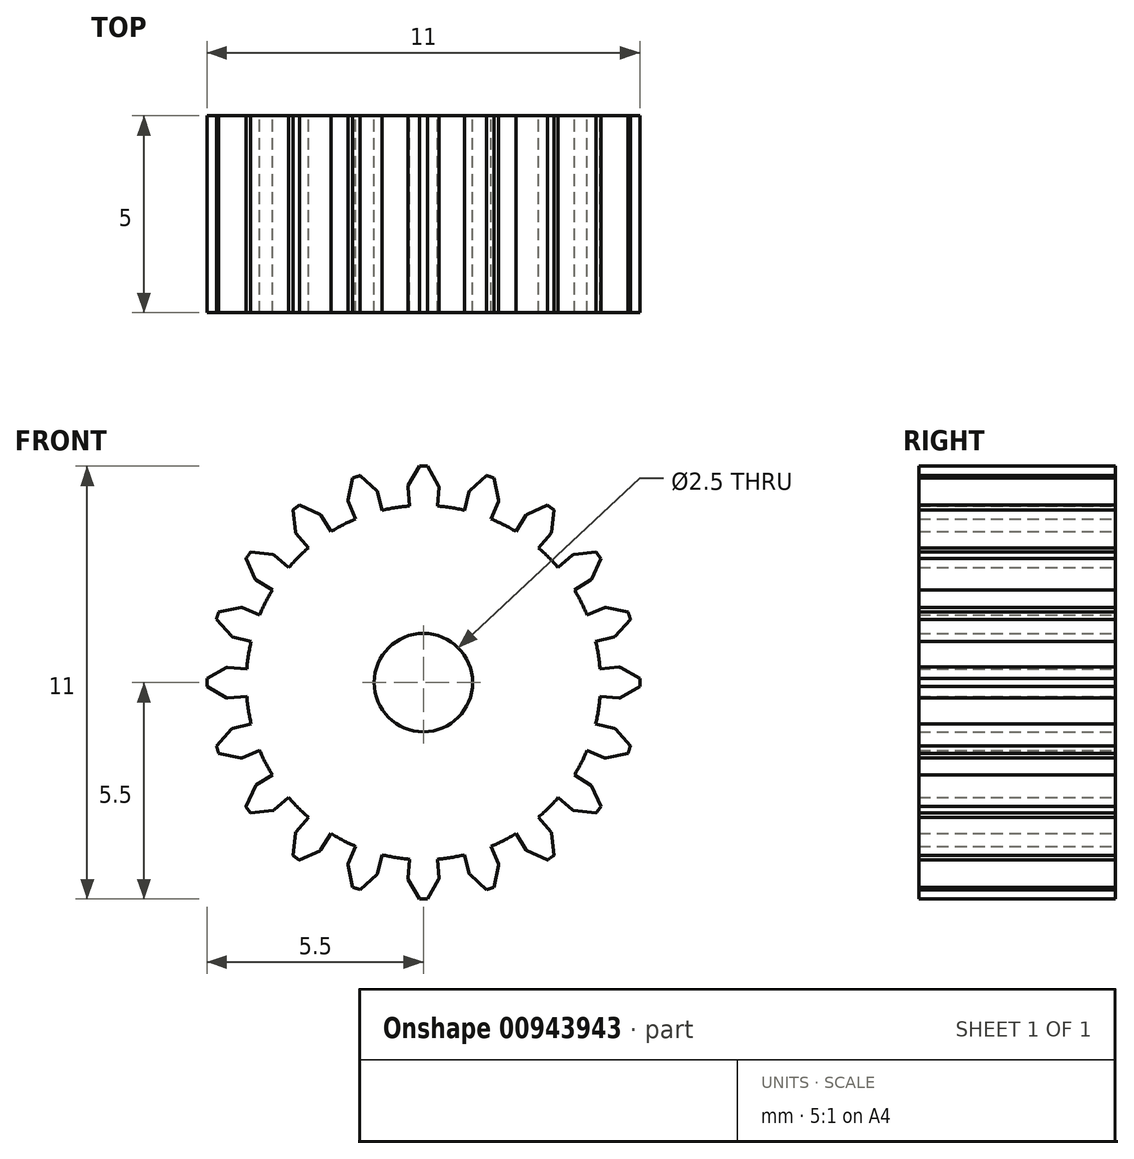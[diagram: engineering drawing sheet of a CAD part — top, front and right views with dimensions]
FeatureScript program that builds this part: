
annotation { "Feature Type Name" : "Feature", "Feature Type Description" : "" }
export const myFeature = defineFeature(function(context is Context, id is Id, definition is map)
    precondition{}
    {
        {
            var Q0;
            Q0=qCreatedBy(makeId("Front.planeOp"),FACE);
            var sketch = newSketch(context, id + "F0", { "sketchPlane" : qUnion([Q0])});
            skCircle(sketch, "E0", {"center": v(0, 0) * mm, "radius": 4.5 * mm});
            skCircle(sketch, "E1", {"center": v(0, 0) * mm, "radius": 5 * mm, "construction": true});
            skCircle(sketch, "E2", {"center": v(0, 0) * mm, "radius": 5.5 * mm, "construction": true});
            skLineSegment(sketch, "E3", {"start": v(0, 0) * mm, "end": v(1.46, 6.08) * mm, "construction": true});
            skArc(sketch, "E4", {"start": v(-0.4, 4.98) * mm, "mid": v(0, 5) * mm, "end": v(0.4, 4.98) * mm, "construction": true});
            skLineSegment(sketch, "E5", {"start": v(-0.35, 4.49) * mm, "end": v(-0.4, 4.98) * mm});
            skArc(sketch, "E6", {"start": v(0, 5.5) * mm, "mid": v(0.05, 5.5) * mm, "end": v(0.1, 5.5) * mm});
            skLineSegment(sketch, "E7", {"start": v(0.1, 5.5) * mm, "end": v(0.38, 5) * mm});
            skLineSegment(sketch, "E8", {"start": v(0.4, 4.98) * mm, "end": v(0.35, 4.49) * mm});
            skLineSegment(sketch, "E9", {"start": v(-0.38, 5) * mm, "end": v(-0.1, 5.5) * mm});
            skArc(sketch, "E10", {"start": v(-0.1, 5.5) * mm, "mid": v(-0.05, 5.5) * mm, "end": v(0, 5.5) * mm});
            skArc(sketch, "E11.filletArc", {"start": v(-0.38, 5) * mm, "mid": v(-0.4, 4.99) * mm, "end": v(-0.4, 4.97) * mm});
            skArc(sketch, "E12.filletArc", {"start": v(0.4, 4.97) * mm, "mid": v(0.4, 4.98) * mm, "end": v(0.38, 5) * mm});
            skLineSegment(sketch, "E13.1.0", {"start": v(-1.91, 4.64) * mm, "end": v(-1.8, 5.2) * mm});
            skLineSegment(sketch, "E13.1.1", {"start": v(-1.6, 5.26) * mm, "end": v(-1.18, 4.87) * mm});
            skArc(sketch, "E13.1.2", {"start": v(-1.8, 5.2) * mm, "mid": v(-1.75, 5.22) * mm, "end": v(-1.7, 5.23) * mm});
            skArc(sketch, "E13.1.3", {"start": v(-1.7, 5.23) * mm, "mid": v(-1.65, 5.25) * mm, "end": v(-1.6, 5.26) * mm});
            skArc(sketch, "E13.1.4", {"start": v(-1.16, 4.85) * mm, "mid": v(-1.17, 4.86) * mm, "end": v(-1.18, 4.87) * mm});
            skArc(sketch, "E13.1.5", {"start": v(-1.91, 4.64) * mm, "mid": v(-1.91, 4.62) * mm, "end": v(-1.9, 4.6) * mm});
            skLineSegment(sketch, "E13.1.6", {"start": v(0, 0) * mm, "end": v(-1.9, 4.6) * mm, "construction": true});
            skLineSegment(sketch, "E13.1.7", {"start": v(0, 0) * mm, "end": v(-1.16, 4.85) * mm, "construction": true});
            skLineSegment(sketch, "E13.2.0", {"start": v(-3.25, 3.82) * mm, "end": v(-3.31, 4.4) * mm});
            skLineSegment(sketch, "E13.2.1", {"start": v(-3.15, 4.5) * mm, "end": v(-2.63, 4.27) * mm});
            skArc(sketch, "E13.2.2", {"start": v(-3.31, 4.4) * mm, "mid": v(-3.27, 4.42) * mm, "end": v(-3.23, 4.45) * mm});
            skArc(sketch, "E13.2.3", {"start": v(-3.23, 4.45) * mm, "mid": v(-3.2, 4.48) * mm, "end": v(-3.15, 4.5) * mm});
            skArc(sketch, "E13.2.4", {"start": v(-2.6, 4.25) * mm, "mid": v(-2.61, 4.26) * mm, "end": v(-2.63, 4.27) * mm});
            skArc(sketch, "E13.2.5", {"start": v(-3.25, 3.82) * mm, "mid": v(-3.25, 3.8) * mm, "end": v(-3.24, 3.8) * mm});
            skLineSegment(sketch, "E13.2.6", {"start": v(0, 0) * mm, "end": v(-3.24, 3.8) * mm, "construction": true});
            skLineSegment(sketch, "E13.2.7", {"start": v(0, 0) * mm, "end": v(-2.6, 4.25) * mm, "construction": true});
            skLineSegment(sketch, "E13.3.0", {"start": v(-4.27, 2.63) * mm, "end": v(-4.5, 3.15) * mm});
            skLineSegment(sketch, "E13.3.1", {"start": v(-4.4, 3.31) * mm, "end": v(-3.82, 3.25) * mm});
            skArc(sketch, "E13.3.2", {"start": v(-4.5, 3.15) * mm, "mid": v(-4.48, 3.2) * mm, "end": v(-4.45, 3.23) * mm});
            skArc(sketch, "E13.3.3", {"start": v(-4.45, 3.23) * mm, "mid": v(-4.42, 3.27) * mm, "end": v(-4.4, 3.31) * mm});
            skArc(sketch, "E13.3.4", {"start": v(-3.8, 3.24) * mm, "mid": v(-3.8, 3.25) * mm, "end": v(-3.82, 3.25) * mm});
            skArc(sketch, "E13.3.5", {"start": v(-4.27, 2.63) * mm, "mid": v(-4.27, 2.62) * mm, "end": v(-4.25, 2.6) * mm});
            skLineSegment(sketch, "E13.3.6", {"start": v(0, 0) * mm, "end": v(-4.25, 2.6) * mm, "construction": true});
            skLineSegment(sketch, "E13.3.7", {"start": v(0, 0) * mm, "end": v(-3.8, 3.24) * mm, "construction": true});
            skLineSegment(sketch, "E13.4.0", {"start": v(-4.88, 1.18) * mm, "end": v(-5.26, 1.6) * mm});
            skLineSegment(sketch, "E13.4.1", {"start": v(-5.2, 1.8) * mm, "end": v(-4.63, 1.91) * mm});
            skArc(sketch, "E13.4.2", {"start": v(-5.26, 1.6) * mm, "mid": v(-5.25, 1.65) * mm, "end": v(-5.23, 1.7) * mm});
            skArc(sketch, "E13.4.3", {"start": v(-5.23, 1.7) * mm, "mid": v(-5.22, 1.75) * mm, "end": v(-5.2, 1.8) * mm});
            skArc(sketch, "E13.4.4", {"start": v(-4.6, 1.9) * mm, "mid": v(-4.62, 1.91) * mm, "end": v(-4.63, 1.91) * mm});
            skArc(sketch, "E13.4.5", {"start": v(-4.88, 1.18) * mm, "mid": v(-4.87, 1.17) * mm, "end": v(-4.85, 1.16) * mm});
            skLineSegment(sketch, "E13.4.6", {"start": v(0, 0) * mm, "end": v(-4.85, 1.16) * mm, "construction": true});
            skLineSegment(sketch, "E13.4.7", {"start": v(0, 0) * mm, "end": v(-4.6, 1.9) * mm, "construction": true});
            skLineSegment(sketch, "E13.5.0", {"start": v(-5, -0.38) * mm, "end": v(-5.5, -0.1) * mm});
            skLineSegment(sketch, "E13.5.1", {"start": v(-5.5, 0.1) * mm, "end": v(-5, 0.38) * mm});
            skArc(sketch, "E13.5.2", {"start": v(-5.5, -0.1) * mm, "mid": v(-5.5, -0.05) * mm, "end": v(-5.5, 0) * mm});
            skArc(sketch, "E13.5.3", {"start": v(-5.5, 0) * mm, "mid": v(-5.5, 0.05) * mm, "end": v(-5.5, 0.1) * mm});
            skArc(sketch, "E13.5.4", {"start": v(-4.97, 0.4) * mm, "mid": v(-4.98, 0.4) * mm, "end": v(-5, 0.38) * mm});
            skArc(sketch, "E13.5.5", {"start": v(-5, -0.38) * mm, "mid": v(-4.99, -0.4) * mm, "end": v(-4.97, -0.4) * mm});
            skLineSegment(sketch, "E13.5.6", {"start": v(0, 0) * mm, "end": v(-4.97, -0.4) * mm, "construction": true});
            skLineSegment(sketch, "E13.5.7", {"start": v(0, 0) * mm, "end": v(-4.97, 0.4) * mm, "construction": true});
            skLineSegment(sketch, "E13.6.0", {"start": v(-4.64, -1.91) * mm, "end": v(-5.2, -1.8) * mm});
            skLineSegment(sketch, "E13.6.1", {"start": v(-5.26, -1.6) * mm, "end": v(-4.87, -1.18) * mm});
            skArc(sketch, "E13.6.2", {"start": v(-5.2, -1.8) * mm, "mid": v(-5.22, -1.75) * mm, "end": v(-5.23, -1.7) * mm});
            skArc(sketch, "E13.6.3", {"start": v(-5.23, -1.7) * mm, "mid": v(-5.25, -1.65) * mm, "end": v(-5.26, -1.6) * mm});
            skArc(sketch, "E13.6.4", {"start": v(-4.85, -1.16) * mm, "mid": v(-4.86, -1.17) * mm, "end": v(-4.87, -1.18) * mm});
            skArc(sketch, "E13.6.5", {"start": v(-4.64, -1.91) * mm, "mid": v(-4.62, -1.91) * mm, "end": v(-4.6, -1.9) * mm});
            skLineSegment(sketch, "E13.6.6", {"start": v(0, 0) * mm, "end": v(-4.6, -1.9) * mm, "construction": true});
            skLineSegment(sketch, "E13.6.7", {"start": v(0, 0) * mm, "end": v(-4.85, -1.16) * mm, "construction": true});
            skLineSegment(sketch, "E13.7.0", {"start": v(-3.82, -3.25) * mm, "end": v(-4.4, -3.31) * mm});
            skLineSegment(sketch, "E13.7.1", {"start": v(-4.5, -3.15) * mm, "end": v(-4.27, -2.63) * mm});
            skArc(sketch, "E13.7.2", {"start": v(-4.4, -3.31) * mm, "mid": v(-4.42, -3.27) * mm, "end": v(-4.45, -3.23) * mm});
            skArc(sketch, "E13.7.3", {"start": v(-4.45, -3.23) * mm, "mid": v(-4.48, -3.2) * mm, "end": v(-4.5, -3.15) * mm});
            skArc(sketch, "E13.7.4", {"start": v(-4.25, -2.6) * mm, "mid": v(-4.26, -2.61) * mm, "end": v(-4.27, -2.63) * mm});
            skArc(sketch, "E13.7.5", {"start": v(-3.82, -3.25) * mm, "mid": v(-3.8, -3.25) * mm, "end": v(-3.8, -3.24) * mm});
            skLineSegment(sketch, "E13.7.6", {"start": v(0, 0) * mm, "end": v(-3.8, -3.24) * mm, "construction": true});
            skLineSegment(sketch, "E13.7.7", {"start": v(0, 0) * mm, "end": v(-4.25, -2.6) * mm, "construction": true});
            skLineSegment(sketch, "E13.8.0", {"start": v(-2.63, -4.27) * mm, "end": v(-3.15, -4.5) * mm});
            skLineSegment(sketch, "E13.8.1", {"start": v(-3.31, -4.4) * mm, "end": v(-3.25, -3.82) * mm});
            skArc(sketch, "E13.8.2", {"start": v(-3.15, -4.5) * mm, "mid": v(-3.2, -4.48) * mm, "end": v(-3.23, -4.45) * mm});
            skArc(sketch, "E13.8.3", {"start": v(-3.23, -4.45) * mm, "mid": v(-3.27, -4.42) * mm, "end": v(-3.31, -4.4) * mm});
            skArc(sketch, "E13.8.4", {"start": v(-3.24, -3.8) * mm, "mid": v(-3.25, -3.8) * mm, "end": v(-3.25, -3.82) * mm});
            skArc(sketch, "E13.8.5", {"start": v(-2.63, -4.27) * mm, "mid": v(-2.62, -4.27) * mm, "end": v(-2.6, -4.25) * mm});
            skLineSegment(sketch, "E13.8.6", {"start": v(0, 0) * mm, "end": v(-2.6, -4.25) * mm, "construction": true});
            skLineSegment(sketch, "E13.8.7", {"start": v(0, 0) * mm, "end": v(-3.24, -3.8) * mm, "construction": true});
            skLineSegment(sketch, "E13.9.0", {"start": v(-1.18, -4.88) * mm, "end": v(-1.6, -5.26) * mm});
            skLineSegment(sketch, "E13.9.1", {"start": v(-1.8, -5.2) * mm, "end": v(-1.91, -4.63) * mm});
            skArc(sketch, "E13.9.2", {"start": v(-1.6, -5.26) * mm, "mid": v(-1.65, -5.25) * mm, "end": v(-1.7, -5.23) * mm});
            skArc(sketch, "E13.9.3", {"start": v(-1.7, -5.23) * mm, "mid": v(-1.75, -5.22) * mm, "end": v(-1.8, -5.2) * mm});
            skArc(sketch, "E13.9.4", {"start": v(-1.9, -4.6) * mm, "mid": v(-1.91, -4.62) * mm, "end": v(-1.91, -4.63) * mm});
            skArc(sketch, "E13.9.5", {"start": v(-1.18, -4.88) * mm, "mid": v(-1.17, -4.87) * mm, "end": v(-1.16, -4.85) * mm});
            skLineSegment(sketch, "E13.9.6", {"start": v(0, 0) * mm, "end": v(-1.16, -4.85) * mm, "construction": true});
            skLineSegment(sketch, "E13.9.7", {"start": v(0, 0) * mm, "end": v(-1.9, -4.6) * mm, "construction": true});
            skLineSegment(sketch, "E13.10.0", {"start": v(0.38, -5) * mm, "end": v(0.1, -5.5) * mm});
            skLineSegment(sketch, "E13.10.1", {"start": v(-0.1, -5.5) * mm, "end": v(-0.38, -5) * mm});
            skArc(sketch, "E13.10.2", {"start": v(0.1, -5.5) * mm, "mid": v(0.05, -5.5) * mm, "end": v(0, -5.5) * mm});
            skArc(sketch, "E13.10.3", {"start": v(0, -5.5) * mm, "mid": v(-0.05, -5.5) * mm, "end": v(-0.1, -5.5) * mm});
            skArc(sketch, "E13.10.4", {"start": v(-0.4, -4.97) * mm, "mid": v(-0.4, -4.98) * mm, "end": v(-0.38, -5) * mm});
            skArc(sketch, "E13.10.5", {"start": v(0.38, -5) * mm, "mid": v(0.4, -4.99) * mm, "end": v(0.4, -4.97) * mm});
            skLineSegment(sketch, "E13.10.6", {"start": v(0, 0) * mm, "end": v(0.4, -4.97) * mm, "construction": true});
            skLineSegment(sketch, "E13.10.7", {"start": v(0, 0) * mm, "end": v(-0.4, -4.97) * mm, "construction": true});
            skLineSegment(sketch, "E13.11.0", {"start": v(1.91, -4.64) * mm, "end": v(1.8, -5.2) * mm});
            skLineSegment(sketch, "E13.11.1", {"start": v(1.6, -5.26) * mm, "end": v(1.18, -4.87) * mm});
            skArc(sketch, "E13.11.2", {"start": v(1.8, -5.2) * mm, "mid": v(1.75, -5.22) * mm, "end": v(1.7, -5.23) * mm});
            skArc(sketch, "E13.11.3", {"start": v(1.7, -5.23) * mm, "mid": v(1.65, -5.25) * mm, "end": v(1.6, -5.26) * mm});
            skArc(sketch, "E13.11.4", {"start": v(1.16, -4.85) * mm, "mid": v(1.17, -4.86) * mm, "end": v(1.18, -4.87) * mm});
            skArc(sketch, "E13.11.5", {"start": v(1.91, -4.64) * mm, "mid": v(1.91, -4.62) * mm, "end": v(1.9, -4.6) * mm});
            skLineSegment(sketch, "E13.11.6", {"start": v(0, 0) * mm, "end": v(1.9, -4.6) * mm, "construction": true});
            skLineSegment(sketch, "E13.11.7", {"start": v(0, 0) * mm, "end": v(1.16, -4.85) * mm, "construction": true});
            skLineSegment(sketch, "E13.12.0", {"start": v(3.25, -3.82) * mm, "end": v(3.31, -4.4) * mm});
            skLineSegment(sketch, "E13.12.1", {"start": v(3.15, -4.5) * mm, "end": v(2.63, -4.27) * mm});
            skArc(sketch, "E13.12.2", {"start": v(3.31, -4.4) * mm, "mid": v(3.27, -4.42) * mm, "end": v(3.23, -4.45) * mm});
            skArc(sketch, "E13.12.3", {"start": v(3.23, -4.45) * mm, "mid": v(3.2, -4.48) * mm, "end": v(3.15, -4.5) * mm});
            skArc(sketch, "E13.12.4", {"start": v(2.6, -4.25) * mm, "mid": v(2.61, -4.26) * mm, "end": v(2.63, -4.27) * mm});
            skArc(sketch, "E13.12.5", {"start": v(3.25, -3.82) * mm, "mid": v(3.25, -3.8) * mm, "end": v(3.24, -3.8) * mm});
            skLineSegment(sketch, "E13.12.6", {"start": v(0, 0) * mm, "end": v(3.24, -3.8) * mm, "construction": true});
            skLineSegment(sketch, "E13.12.7", {"start": v(0, 0) * mm, "end": v(2.6, -4.25) * mm, "construction": true});
            skLineSegment(sketch, "E13.13.0", {"start": v(4.27, -2.63) * mm, "end": v(4.5, -3.15) * mm});
            skLineSegment(sketch, "E13.13.1", {"start": v(4.4, -3.31) * mm, "end": v(3.82, -3.25) * mm});
            skArc(sketch, "E13.13.2", {"start": v(4.5, -3.15) * mm, "mid": v(4.48, -3.2) * mm, "end": v(4.45, -3.23) * mm});
            skArc(sketch, "E13.13.3", {"start": v(4.45, -3.23) * mm, "mid": v(4.42, -3.27) * mm, "end": v(4.4, -3.31) * mm});
            skArc(sketch, "E13.13.4", {"start": v(3.8, -3.24) * mm, "mid": v(3.8, -3.25) * mm, "end": v(3.82, -3.25) * mm});
            skArc(sketch, "E13.13.5", {"start": v(4.27, -2.63) * mm, "mid": v(4.27, -2.62) * mm, "end": v(4.25, -2.6) * mm});
            skLineSegment(sketch, "E13.13.6", {"start": v(0, 0) * mm, "end": v(4.25, -2.6) * mm, "construction": true});
            skLineSegment(sketch, "E13.13.7", {"start": v(0, 0) * mm, "end": v(3.8, -3.24) * mm, "construction": true});
            skLineSegment(sketch, "E13.14.0", {"start": v(4.88, -1.18) * mm, "end": v(5.26, -1.6) * mm});
            skLineSegment(sketch, "E13.14.1", {"start": v(5.2, -1.8) * mm, "end": v(4.63, -1.91) * mm});
            skArc(sketch, "E13.14.2", {"start": v(5.26, -1.6) * mm, "mid": v(5.25, -1.65) * mm, "end": v(5.23, -1.7) * mm});
            skArc(sketch, "E13.14.3", {"start": v(5.23, -1.7) * mm, "mid": v(5.22, -1.75) * mm, "end": v(5.2, -1.8) * mm});
            skArc(sketch, "E13.14.4", {"start": v(4.6, -1.9) * mm, "mid": v(4.62, -1.91) * mm, "end": v(4.63, -1.91) * mm});
            skArc(sketch, "E13.14.5", {"start": v(4.88, -1.18) * mm, "mid": v(4.87, -1.17) * mm, "end": v(4.85, -1.16) * mm});
            skLineSegment(sketch, "E13.14.6", {"start": v(0, 0) * mm, "end": v(4.85, -1.16) * mm, "construction": true});
            skLineSegment(sketch, "E13.14.7", {"start": v(0, 0) * mm, "end": v(4.6, -1.9) * mm, "construction": true});
            skLineSegment(sketch, "E13.15.0", {"start": v(5, 0.38) * mm, "end": v(5.5, 0.1) * mm});
            skLineSegment(sketch, "E13.15.1", {"start": v(5.5, -0.1) * mm, "end": v(5, -0.38) * mm});
            skArc(sketch, "E13.15.2", {"start": v(5.5, 0.1) * mm, "mid": v(5.5, 0.05) * mm, "end": v(5.5, 0) * mm});
            skArc(sketch, "E13.15.3", {"start": v(5.5, 0) * mm, "mid": v(5.5, -0.05) * mm, "end": v(5.5, -0.1) * mm});
            skArc(sketch, "E13.15.4", {"start": v(4.97, -0.4) * mm, "mid": v(4.98, -0.4) * mm, "end": v(5, -0.38) * mm});
            skArc(sketch, "E13.15.5", {"start": v(5, 0.38) * mm, "mid": v(4.99, 0.4) * mm, "end": v(4.97, 0.4) * mm});
            skLineSegment(sketch, "E13.15.6", {"start": v(0, 0) * mm, "end": v(4.97, 0.4) * mm, "construction": true});
            skLineSegment(sketch, "E13.15.7", {"start": v(0, 0) * mm, "end": v(4.97, -0.4) * mm, "construction": true});
            skLineSegment(sketch, "E13.16.0", {"start": v(4.64, 1.91) * mm, "end": v(5.2, 1.8) * mm});
            skLineSegment(sketch, "E13.16.1", {"start": v(5.26, 1.6) * mm, "end": v(4.87, 1.18) * mm});
            skArc(sketch, "E13.16.2", {"start": v(5.2, 1.8) * mm, "mid": v(5.22, 1.75) * mm, "end": v(5.23, 1.7) * mm});
            skArc(sketch, "E13.16.3", {"start": v(5.23, 1.7) * mm, "mid": v(5.25, 1.65) * mm, "end": v(5.26, 1.6) * mm});
            skArc(sketch, "E13.16.4", {"start": v(4.85, 1.16) * mm, "mid": v(4.86, 1.17) * mm, "end": v(4.87, 1.18) * mm});
            skArc(sketch, "E13.16.5", {"start": v(4.64, 1.91) * mm, "mid": v(4.62, 1.91) * mm, "end": v(4.6, 1.9) * mm});
            skLineSegment(sketch, "E13.16.6", {"start": v(0, 0) * mm, "end": v(4.6, 1.9) * mm, "construction": true});
            skLineSegment(sketch, "E13.16.7", {"start": v(0, 0) * mm, "end": v(4.85, 1.16) * mm, "construction": true});
            skLineSegment(sketch, "E13.17.0", {"start": v(3.82, 3.25) * mm, "end": v(4.4, 3.31) * mm});
            skLineSegment(sketch, "E13.17.1", {"start": v(4.5, 3.15) * mm, "end": v(4.27, 2.63) * mm});
            skArc(sketch, "E13.17.2", {"start": v(4.4, 3.31) * mm, "mid": v(4.42, 3.27) * mm, "end": v(4.45, 3.23) * mm});
            skArc(sketch, "E13.17.3", {"start": v(4.45, 3.23) * mm, "mid": v(4.48, 3.2) * mm, "end": v(4.5, 3.15) * mm});
            skArc(sketch, "E13.17.4", {"start": v(4.25, 2.6) * mm, "mid": v(4.26, 2.61) * mm, "end": v(4.27, 2.63) * mm});
            skArc(sketch, "E13.17.5", {"start": v(3.82, 3.25) * mm, "mid": v(3.8, 3.25) * mm, "end": v(3.8, 3.24) * mm});
            skLineSegment(sketch, "E13.17.6", {"start": v(0, 0) * mm, "end": v(3.8, 3.24) * mm, "construction": true});
            skLineSegment(sketch, "E13.17.7", {"start": v(0, 0) * mm, "end": v(4.25, 2.6) * mm, "construction": true});
            skLineSegment(sketch, "E13.18.0", {"start": v(2.63, 4.27) * mm, "end": v(3.15, 4.5) * mm});
            skLineSegment(sketch, "E13.18.1", {"start": v(3.31, 4.4) * mm, "end": v(3.25, 3.82) * mm});
            skArc(sketch, "E13.18.2", {"start": v(3.15, 4.5) * mm, "mid": v(3.2, 4.48) * mm, "end": v(3.23, 4.45) * mm});
            skArc(sketch, "E13.18.3", {"start": v(3.23, 4.45) * mm, "mid": v(3.27, 4.42) * mm, "end": v(3.31, 4.4) * mm});
            skArc(sketch, "E13.18.4", {"start": v(3.24, 3.8) * mm, "mid": v(3.25, 3.8) * mm, "end": v(3.25, 3.82) * mm});
            skArc(sketch, "E13.18.5", {"start": v(2.63, 4.27) * mm, "mid": v(2.62, 4.27) * mm, "end": v(2.6, 4.25) * mm});
            skLineSegment(sketch, "E13.18.6", {"start": v(0, 0) * mm, "end": v(2.6, 4.25) * mm, "construction": true});
            skLineSegment(sketch, "E13.18.7", {"start": v(0, 0) * mm, "end": v(3.24, 3.8) * mm, "construction": true});
            skLineSegment(sketch, "E13.19.0", {"start": v(1.18, 4.88) * mm, "end": v(1.6, 5.26) * mm});
            skLineSegment(sketch, "E13.19.1", {"start": v(1.8, 5.2) * mm, "end": v(1.91, 4.63) * mm});
            skArc(sketch, "E13.19.2", {"start": v(1.6, 5.26) * mm, "mid": v(1.65, 5.25) * mm, "end": v(1.7, 5.23) * mm});
            skArc(sketch, "E13.19.3", {"start": v(1.7, 5.23) * mm, "mid": v(1.75, 5.22) * mm, "end": v(1.8, 5.2) * mm});
            skArc(sketch, "E13.19.4", {"start": v(1.9, 4.6) * mm, "mid": v(1.91, 4.62) * mm, "end": v(1.91, 4.63) * mm});
            skArc(sketch, "E13.19.5", {"start": v(1.18, 4.88) * mm, "mid": v(1.17, 4.87) * mm, "end": v(1.16, 4.85) * mm});
            skLineSegment(sketch, "E13.19.6", {"start": v(0, 0) * mm, "end": v(1.16, 4.85) * mm, "construction": true});
            skLineSegment(sketch, "E13.19.7", {"start": v(0, 0) * mm, "end": v(1.9, 4.6) * mm, "construction": true});
            skLineSegment(sketch, "E14.1.0", {"start": v(-1.72, 4.16) * mm, "end": v(-1.91, 4.62) * mm});
            skLineSegment(sketch, "E14.1.1", {"start": v(-1.17, 4.86) * mm, "end": v(-1.05, 4.38) * mm});
            skLineSegment(sketch, "E14.2.0", {"start": v(-2.92, 3.42) * mm, "end": v(-3.25, 3.8) * mm});
            skLineSegment(sketch, "E14.2.1", {"start": v(-2.61, 4.26) * mm, "end": v(-2.35, 3.84) * mm});
            skLineSegment(sketch, "E14.3.0", {"start": v(-3.84, 2.35) * mm, "end": v(-4.26, 2.61) * mm});
            skLineSegment(sketch, "E14.3.1", {"start": v(-3.8, 3.25) * mm, "end": v(-3.42, 2.92) * mm});
            skLineSegment(sketch, "E14.4.0", {"start": v(-4.38, 1.05) * mm, "end": v(-4.86, 1.17) * mm});
            skLineSegment(sketch, "E14.4.1", {"start": v(-4.62, 1.91) * mm, "end": v(-4.16, 1.72) * mm});
            skLineSegment(sketch, "E14.5.0", {"start": v(-4.49, -0.35) * mm, "end": v(-4.98, -0.4) * mm});
            skLineSegment(sketch, "E14.5.1", {"start": v(-4.98, 0.4) * mm, "end": v(-4.49, 0.35) * mm});
            skLineSegment(sketch, "E14.6.0", {"start": v(-4.16, -1.72) * mm, "end": v(-4.62, -1.91) * mm});
            skLineSegment(sketch, "E14.6.1", {"start": v(-4.86, -1.17) * mm, "end": v(-4.38, -1.05) * mm});
            skLineSegment(sketch, "E14.7.0", {"start": v(-3.42, -2.92) * mm, "end": v(-3.8, -3.25) * mm});
            skLineSegment(sketch, "E14.7.1", {"start": v(-4.26, -2.61) * mm, "end": v(-3.84, -2.35) * mm});
            skLineSegment(sketch, "E14.8.0", {"start": v(-2.35, -3.84) * mm, "end": v(-2.61, -4.26) * mm});
            skLineSegment(sketch, "E14.8.1", {"start": v(-3.25, -3.8) * mm, "end": v(-2.92, -3.42) * mm});
            skLineSegment(sketch, "E14.9.0", {"start": v(-1.05, -4.38) * mm, "end": v(-1.17, -4.86) * mm});
            skLineSegment(sketch, "E14.9.1", {"start": v(-1.91, -4.62) * mm, "end": v(-1.72, -4.16) * mm});
            skLineSegment(sketch, "E14.10.0", {"start": v(0.35, -4.49) * mm, "end": v(0.4, -4.98) * mm});
            skLineSegment(sketch, "E14.10.1", {"start": v(-0.4, -4.98) * mm, "end": v(-0.35, -4.49) * mm});
            skLineSegment(sketch, "E14.11.0", {"start": v(1.72, -4.16) * mm, "end": v(1.91, -4.62) * mm});
            skLineSegment(sketch, "E14.11.1", {"start": v(1.17, -4.86) * mm, "end": v(1.05, -4.38) * mm});
            skLineSegment(sketch, "E14.12.0", {"start": v(2.92, -3.42) * mm, "end": v(3.25, -3.8) * mm});
            skLineSegment(sketch, "E14.12.1", {"start": v(2.61, -4.26) * mm, "end": v(2.35, -3.84) * mm});
            skLineSegment(sketch, "E14.13.0", {"start": v(3.84, -2.35) * mm, "end": v(4.26, -2.61) * mm});
            skLineSegment(sketch, "E14.13.1", {"start": v(3.8, -3.25) * mm, "end": v(3.42, -2.92) * mm});
            skLineSegment(sketch, "E14.14.0", {"start": v(4.38, -1.05) * mm, "end": v(4.86, -1.17) * mm});
            skLineSegment(sketch, "E14.14.1", {"start": v(4.62, -1.91) * mm, "end": v(4.16, -1.72) * mm});
            skLineSegment(sketch, "E14.15.0", {"start": v(4.49, 0.35) * mm, "end": v(4.98, 0.4) * mm});
            skLineSegment(sketch, "E14.15.1", {"start": v(4.98, -0.4) * mm, "end": v(4.49, -0.35) * mm});
            skLineSegment(sketch, "E14.16.0", {"start": v(4.16, 1.72) * mm, "end": v(4.62, 1.91) * mm});
            skLineSegment(sketch, "E14.16.1", {"start": v(4.86, 1.17) * mm, "end": v(4.38, 1.05) * mm});
            skLineSegment(sketch, "E14.17.0", {"start": v(3.42, 2.92) * mm, "end": v(3.8, 3.25) * mm});
            skLineSegment(sketch, "E14.17.1", {"start": v(4.26, 2.61) * mm, "end": v(3.84, 2.35) * mm});
            skLineSegment(sketch, "E14.18.0", {"start": v(2.35, 3.84) * mm, "end": v(2.61, 4.26) * mm});
            skLineSegment(sketch, "E14.18.1", {"start": v(3.25, 3.8) * mm, "end": v(2.92, 3.42) * mm});
            skLineSegment(sketch, "E14.19.0", {"start": v(1.05, 4.38) * mm, "end": v(1.17, 4.86) * mm});
            skLineSegment(sketch, "E14.19.1", {"start": v(1.91, 4.62) * mm, "end": v(1.72, 4.16) * mm});
            skSolve(sketch);
        }
        {
            var Q0;
            Q0 = qSketchRegion(id + "F0", true);
            extrude(context, id + "F1", {"entities" : qUnion([Q0]), "depth" : 5 * mm, "offsetDistance" : 25 * mm});
        }
        {
            var Q0;
            Q0=sQuery(id+"F0.wireOp",VERTEX,"E0.center");
            var Q1;
            Q1=makeQuery(id+"F1.opExtrude","SWEPT_BODY",BODY,{"disambiguationData":[OSD([sQuery(id+"F0.wireOp",EDGE,"E0"),sQuery(id+"F0.wireOp",EDGE,"E5"),sQuery(id+"F0.wireOp",EDGE,"E6"),sQuery(id+"F0.wireOp",EDGE,"E7"),sQuery(id+"F0.wireOp",EDGE,"E8"),sQuery(id+"F0.wireOp",EDGE,"E9"),sQuery(id+"F0.wireOp",EDGE,"E10"),sQuery(id+"F0.wireOp",EDGE,"E11.filletArc"),sQuery(id+"F0.wireOp",EDGE,"E12.filletArc"),sQuery(id+"F0.wireOp",EDGE,"E13.1.0"),sQuery(id+"F0.wireOp",EDGE,"E13.1.1"),sQuery(id+"F0.wireOp",EDGE,"E13.1.2"),sQuery(id+"F0.wireOp",EDGE,"E13.1.3"),sQuery(id+"F0.wireOp",EDGE,"E13.1.4"),sQuery(id+"F0.wireOp",EDGE,"E13.1.5"),sQuery(id+"F0.wireOp",EDGE,"E13.2.0"),sQuery(id+"F0.wireOp",EDGE,"E13.2.1"),sQuery(id+"F0.wireOp",EDGE,"E13.2.2"),sQuery(id+"F0.wireOp",EDGE,"E13.2.3"),sQuery(id+"F0.wireOp",EDGE,"E13.2.4"),sQuery(id+"F0.wireOp",EDGE,"E13.2.5"),sQuery(id+"F0.wireOp",EDGE,"E13.3.0"),sQuery(id+"F0.wireOp",EDGE,"E13.3.1"),sQuery(id+"F0.wireOp",EDGE,"E13.3.2"),sQuery(id+"F0.wireOp",EDGE,"E13.3.3"),sQuery(id+"F0.wireOp",EDGE,"E13.3.4"),sQuery(id+"F0.wireOp",EDGE,"E13.3.5"),sQuery(id+"F0.wireOp",EDGE,"E13.4.0"),sQuery(id+"F0.wireOp",EDGE,"E13.4.1"),sQuery(id+"F0.wireOp",EDGE,"E13.4.2"),sQuery(id+"F0.wireOp",EDGE,"E13.4.3"),sQuery(id+"F0.wireOp",EDGE,"E13.4.4"),sQuery(id+"F0.wireOp",EDGE,"E13.4.5"),sQuery(id+"F0.wireOp",EDGE,"E13.5.0"),sQuery(id+"F0.wireOp",EDGE,"E13.5.1"),sQuery(id+"F0.wireOp",EDGE,"E13.5.2"),sQuery(id+"F0.wireOp",EDGE,"E13.5.3"),sQuery(id+"F0.wireOp",EDGE,"E13.5.4"),sQuery(id+"F0.wireOp",EDGE,"E13.5.5"),sQuery(id+"F0.wireOp",EDGE,"E13.6.0"),sQuery(id+"F0.wireOp",EDGE,"E13.6.1"),sQuery(id+"F0.wireOp",EDGE,"E13.6.2"),sQuery(id+"F0.wireOp",EDGE,"E13.6.3"),sQuery(id+"F0.wireOp",EDGE,"E13.6.4"),sQuery(id+"F0.wireOp",EDGE,"E13.6.5"),sQuery(id+"F0.wireOp",EDGE,"E13.7.0"),sQuery(id+"F0.wireOp",EDGE,"E13.7.1"),sQuery(id+"F0.wireOp",EDGE,"E13.7.2"),sQuery(id+"F0.wireOp",EDGE,"E13.7.3"),sQuery(id+"F0.wireOp",EDGE,"E13.7.4"),sQuery(id+"F0.wireOp",EDGE,"E13.7.5"),sQuery(id+"F0.wireOp",EDGE,"E13.8.0"),sQuery(id+"F0.wireOp",EDGE,"E13.8.1"),sQuery(id+"F0.wireOp",EDGE,"E13.8.2"),sQuery(id+"F0.wireOp",EDGE,"E13.8.3"),sQuery(id+"F0.wireOp",EDGE,"E13.8.4"),sQuery(id+"F0.wireOp",EDGE,"E13.8.5"),sQuery(id+"F0.wireOp",EDGE,"E13.9.0"),sQuery(id+"F0.wireOp",EDGE,"E13.9.1"),sQuery(id+"F0.wireOp",EDGE,"E13.9.2"),sQuery(id+"F0.wireOp",EDGE,"E13.9.3"),sQuery(id+"F0.wireOp",EDGE,"E13.9.4"),sQuery(id+"F0.wireOp",EDGE,"E13.9.5"),sQuery(id+"F0.wireOp",EDGE,"E13.10.0"),sQuery(id+"F0.wireOp",EDGE,"E13.10.1"),sQuery(id+"F0.wireOp",EDGE,"E13.10.2"),sQuery(id+"F0.wireOp",EDGE,"E13.10.3"),sQuery(id+"F0.wireOp",EDGE,"E13.10.4"),sQuery(id+"F0.wireOp",EDGE,"E13.10.5"),sQuery(id+"F0.wireOp",EDGE,"E13.11.0"),sQuery(id+"F0.wireOp",EDGE,"E13.11.1"),sQuery(id+"F0.wireOp",EDGE,"E13.11.2"),sQuery(id+"F0.wireOp",EDGE,"E13.11.3"),sQuery(id+"F0.wireOp",EDGE,"E13.11.4"),sQuery(id+"F0.wireOp",EDGE,"E13.11.5"),sQuery(id+"F0.wireOp",EDGE,"E13.12.0"),sQuery(id+"F0.wireOp",EDGE,"E13.12.1"),sQuery(id+"F0.wireOp",EDGE,"E13.12.2"),sQuery(id+"F0.wireOp",EDGE,"E13.12.3"),sQuery(id+"F0.wireOp",EDGE,"E13.12.4"),sQuery(id+"F0.wireOp",EDGE,"E13.12.5"),sQuery(id+"F0.wireOp",EDGE,"E13.13.0"),sQuery(id+"F0.wireOp",EDGE,"E13.13.1"),sQuery(id+"F0.wireOp",EDGE,"E13.13.2"),sQuery(id+"F0.wireOp",EDGE,"E13.13.3"),sQuery(id+"F0.wireOp",EDGE,"E13.13.4"),sQuery(id+"F0.wireOp",EDGE,"E13.13.5"),sQuery(id+"F0.wireOp",EDGE,"E13.14.0"),sQuery(id+"F0.wireOp",EDGE,"E13.14.1"),sQuery(id+"F0.wireOp",EDGE,"E13.14.2"),sQuery(id+"F0.wireOp",EDGE,"E13.14.3"),sQuery(id+"F0.wireOp",EDGE,"E13.14.4"),sQuery(id+"F0.wireOp",EDGE,"E13.14.5"),sQuery(id+"F0.wireOp",EDGE,"E13.15.0"),sQuery(id+"F0.wireOp",EDGE,"E13.15.1"),sQuery(id+"F0.wireOp",EDGE,"E13.15.2"),sQuery(id+"F0.wireOp",EDGE,"E13.15.3"),sQuery(id+"F0.wireOp",EDGE,"E13.15.4"),sQuery(id+"F0.wireOp",EDGE,"E13.15.5"),sQuery(id+"F0.wireOp",EDGE,"E13.16.0"),sQuery(id+"F0.wireOp",EDGE,"E13.16.1"),sQuery(id+"F0.wireOp",EDGE,"E13.16.2"),sQuery(id+"F0.wireOp",EDGE,"E13.16.3"),sQuery(id+"F0.wireOp",EDGE,"E13.16.4"),sQuery(id+"F0.wireOp",EDGE,"E13.16.5"),sQuery(id+"F0.wireOp",EDGE,"E13.17.0"),sQuery(id+"F0.wireOp",EDGE,"E13.17.1"),sQuery(id+"F0.wireOp",EDGE,"E13.17.2"),sQuery(id+"F0.wireOp",EDGE,"E13.17.3"),sQuery(id+"F0.wireOp",EDGE,"E13.17.4"),sQuery(id+"F0.wireOp",EDGE,"E13.17.5"),sQuery(id+"F0.wireOp",EDGE,"E13.18.0"),sQuery(id+"F0.wireOp",EDGE,"E13.18.1"),sQuery(id+"F0.wireOp",EDGE,"E13.18.2"),sQuery(id+"F0.wireOp",EDGE,"E13.18.3"),sQuery(id+"F0.wireOp",EDGE,"E13.18.4"),sQuery(id+"F0.wireOp",EDGE,"E13.18.5"),sQuery(id+"F0.wireOp",EDGE,"E13.19.0"),sQuery(id+"F0.wireOp",EDGE,"E13.19.1"),sQuery(id+"F0.wireOp",EDGE,"E13.19.2"),sQuery(id+"F0.wireOp",EDGE,"E13.19.3"),sQuery(id+"F0.wireOp",EDGE,"E13.19.4"),sQuery(id+"F0.wireOp",EDGE,"E13.19.5"),sQuery(id+"F0.wireOp",EDGE,"E14.1.0"),sQuery(id+"F0.wireOp",EDGE,"E14.1.1"),sQuery(id+"F0.wireOp",EDGE,"E14.2.0"),sQuery(id+"F0.wireOp",EDGE,"E14.2.1"),sQuery(id+"F0.wireOp",EDGE,"E14.3.0"),sQuery(id+"F0.wireOp",EDGE,"E14.3.1"),sQuery(id+"F0.wireOp",EDGE,"E14.4.0"),sQuery(id+"F0.wireOp",EDGE,"E14.4.1"),sQuery(id+"F0.wireOp",EDGE,"E14.5.0"),sQuery(id+"F0.wireOp",EDGE,"E14.5.1"),sQuery(id+"F0.wireOp",EDGE,"E14.6.0"),sQuery(id+"F0.wireOp",EDGE,"E14.6.1"),sQuery(id+"F0.wireOp",EDGE,"E14.7.0"),sQuery(id+"F0.wireOp",EDGE,"E14.7.1"),sQuery(id+"F0.wireOp",EDGE,"E14.8.0"),sQuery(id+"F0.wireOp",EDGE,"E14.8.1"),sQuery(id+"F0.wireOp",EDGE,"E14.9.0"),sQuery(id+"F0.wireOp",EDGE,"E14.9.1"),sQuery(id+"F0.wireOp",EDGE,"E14.10.0"),sQuery(id+"F0.wireOp",EDGE,"E14.10.1"),sQuery(id+"F0.wireOp",EDGE,"E14.11.0"),sQuery(id+"F0.wireOp",EDGE,"E14.11.1"),sQuery(id+"F0.wireOp",EDGE,"E14.12.0"),sQuery(id+"F0.wireOp",EDGE,"E14.12.1"),sQuery(id+"F0.wireOp",EDGE,"E14.13.0"),sQuery(id+"F0.wireOp",EDGE,"E14.13.1"),sQuery(id+"F0.wireOp",EDGE,"E14.14.0"),sQuery(id+"F0.wireOp",EDGE,"E14.14.1"),sQuery(id+"F0.wireOp",EDGE,"E14.15.0"),sQuery(id+"F0.wireOp",EDGE,"E14.15.1"),sQuery(id+"F0.wireOp",EDGE,"E14.16.0"),sQuery(id+"F0.wireOp",EDGE,"E14.16.1"),sQuery(id+"F0.wireOp",EDGE,"E14.17.0"),sQuery(id+"F0.wireOp",EDGE,"E14.17.1"),sQuery(id+"F0.wireOp",EDGE,"E14.18.0"),sQuery(id+"F0.wireOp",EDGE,"E14.18.1"),sQuery(id+"F0.wireOp",EDGE,"E14.19.0"),sQuery(id+"F0.wireOp",EDGE,"E14.19.1")])]});
            hole(context, id + "F2", {"style" : HoleStyle.SIMPLE, "endStyle" : HoleEndStyle.THROUGH, "oppositeDirection" : true, "holeDiameter" : 2.5 * mm, "majorDiameter" : 5 * mm, "isTappedThrough" : true, "tappedDepth" : 12 * mm, "tapClearance" : 3, "locations" : qUnion([Q0]), "scope" : qUnion([Q1])});
        }
    });
